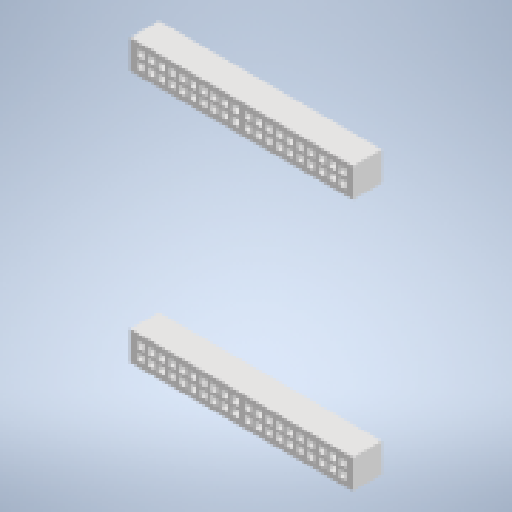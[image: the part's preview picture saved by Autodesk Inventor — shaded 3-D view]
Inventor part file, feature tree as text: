
AUTODESK INVENTOR PART (.ipt)
format: ipt  version: 2024.2 (Build 282272000, 272)  size: 900,096 bytes
history: native  units: mm
features: thread x8, reference x7, other x7, sketch x6, extrude x6, projected_geometry x4, plane x2, fillet x1
ambient origin geometry x8: Origin, YZ Plane, XZ Plane, XY Plane, X Axis, Y Axis, Z Axis, Center Point
bodies: Body1 (feature_tree)
feature tree (41):
  sketch  "Sketch1"  dims[d0=1.2mm d3=1.2mm]
  plane  "Work Plane1"
  extrude  "Extrusion4"  Depth=1.2mm
  extrude  "Extrusion5"  Depth=1.0mm
  extrude  "Extrusion6"  Depth=3.0mm TaperAngle=0.0deg
  fillet  "Fillet1"  Radius=7.5mm
  sketch  "Sketch7"  dims[d15=7.5mm d16=7.5mm]
  plane  "Work Plane2"
  extrude  "Extrusion7"  Depth=7.5mm
  extrude  "Extrusion8"  Depth=27.0mm
  extrude  "Extrusion9"  Depth=7.0mm
  thread  "Thread1"  [1 undecoded]
  thread  "Thread2"  [1 undecoded]
  thread  "Thread3"  [1 undecoded]
  thread  "Thread4"  [1 undecoded]
  thread  "Thread5"  [1 undecoded]
  thread  "Thread6"  [1 undecoded]
  thread  "Thread7"  [1 undecoded]
  thread  "Thread8"  [1 undecoded]
  sketch  "Sketch5"  dims[d8=1.0mm d9=1.0mm]
  reference  "Reference9"
  reference  "Reference10"
  reference  "Reference11"
  reference  "Reference12"
  projected_geometry  "Projected Loop1"
  projected_geometry  "Projected Loop2"
  sketch  "Sketch6"  dims[d10=7.0mm d11=0.0mm d12=3.0mm d13=0.0mm d14=7.5mm]
  reference  "Reference13"
  reference  "Reference14"
  reference  "Reference15"
  projected_geometry  "Projected Loop3"
  projected_geometry  "Projected Loop4"
  sketch  "Sketch8"  dims[d17=3.0mm d18=0.0mm d19=27.0mm]
  sketch  "Sketch9"  dims[d20=7.0mm d21=7.0mm d22=7.0mm d23=3.0mm d24=0.0mm d25=3.5mm d26=3.5mm d27=3.5mm d28=3.5mm d29=10.0mm d30=0.0mm d31=3.2mm d32=10.0mm d33=3.2mm d34=10.0mm d35=0.0mm d36=0.0mm d37=1.0mm d38=0.0mm d39=1.0mm d40=0.0mm d41=1.0mm d42=0.0mm d43=1.0mm d44=0.0mm d45=1.0mm d46=0.0mm d47=1.0mm d48=0.0mm d49=1.0mm d50=0.0mm d51=1.0mm d52=0.0mm d1=0.5mm d2=0.872665mm d4=0.872665mm]
  other  "<userpath>\Desktop\meca_robotbebou\iks01A2\iks01A2switch.iam"
  other  "iks01A2switch.iam"
  other  "zl262-20d_p2-54_l25-9_w5_h8-5:2"
  other  "zl262-20d_p2-54_l25-9_w5_h8-5:1"
  other  "zl262-20d_p2-54_l25-9_w5_h8-5:4"
  other  "zl262-20d_p2-54_l25-9_w5_h8-5:3"
  other  "NUCLEO-F411RE:1"
note: 8 required parameter values undecoded (feature->parameter linkage not recoverable at this tier; creation-order binding heuristic only, values carry confidence <= 0.55)
